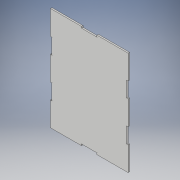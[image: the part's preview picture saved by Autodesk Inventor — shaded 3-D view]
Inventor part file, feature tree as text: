
AUTODESK INVENTOR PART (.ipt)
format: ipt  version: 2017 (Build 210142000, 142)  size: 142,848 bytes
history: native  units: in
note: dims shown in document units (in); Inventor stores cm internally (conversion verified against a paired STEP export)
features: extrude x1, sketch x1
ambient origin geometry x8: Origin, YZ Plane, XZ Plane, XY Plane, X Axis, Y Axis, Z Axis, Center Point
bodies: Solid1 (feature_tree)
feature tree (2):
  extrude  "Extrusion1"  Depth=5.9055in
  sketch  "Sketch1"  dims[d1=7.874in d2=5.9055in d3=2.3622in d4=1.1811in d5=2.3622in d6=0.1181in d26=1.1811in d27=2.3622in d28=2.3622in d29=1.1811in d30=1.1811in d31=0.1181in d32=0.1181in d34=0.1181in d35=0.1181in d36=1.8346in d37=1.8346in d38=1.8346in d39=1.8346in d40=1.8346in d41=1.8346in d42=0.1181in d43=0.0in d44=0.1181in d45=0.1181in d46=0.1181in d47=0.1181in]
